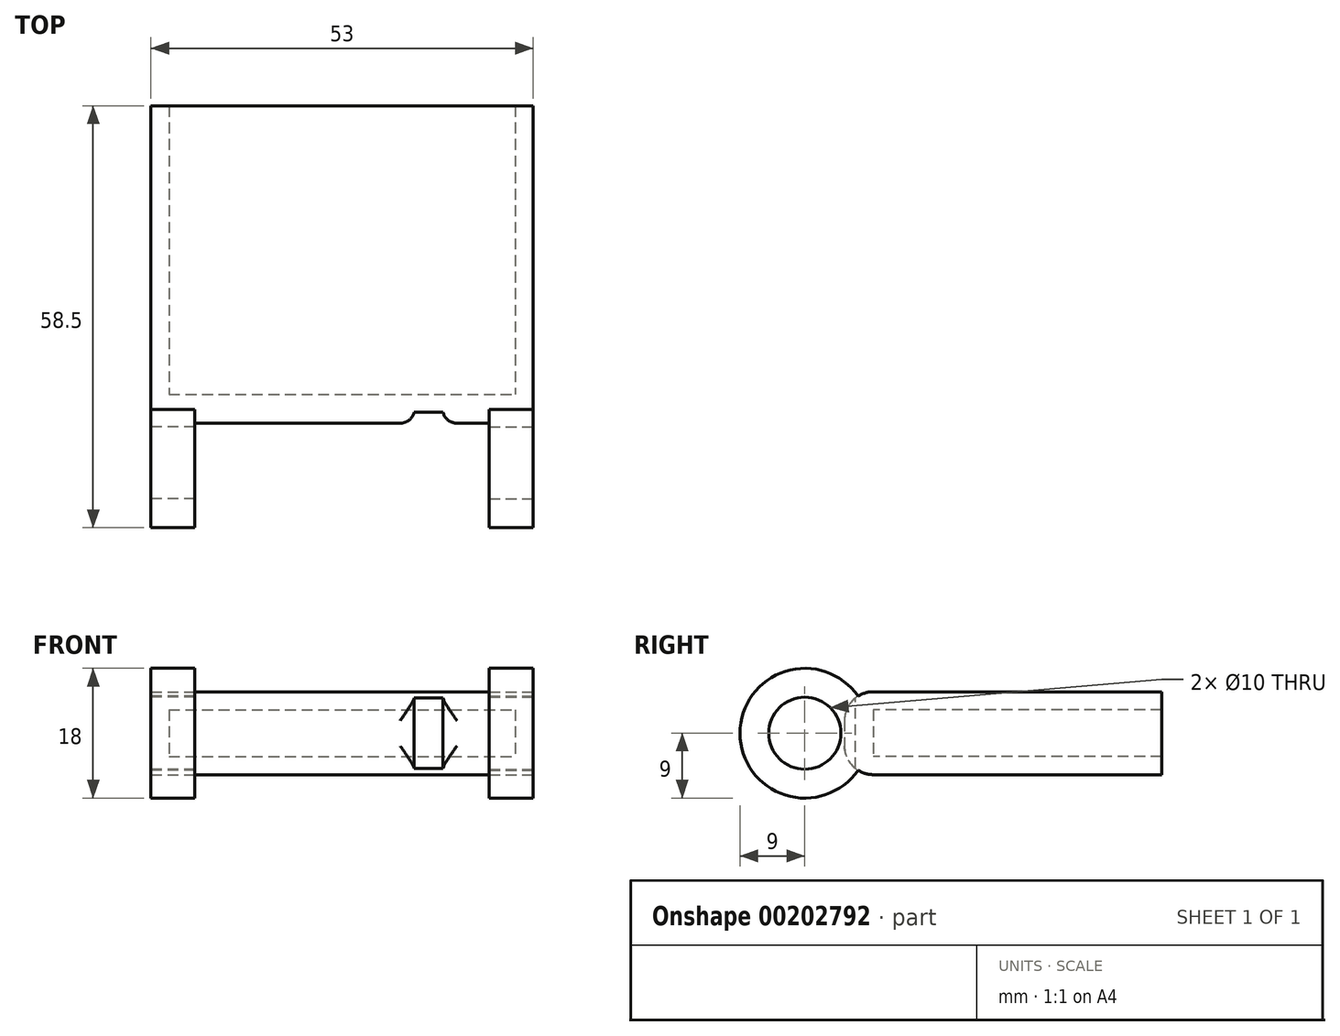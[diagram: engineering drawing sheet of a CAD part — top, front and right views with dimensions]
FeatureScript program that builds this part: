
annotation { "Feature Type Name" : "Feature", "Feature Type Description" : "" }
export const myFeature = defineFeature(function(context is Context, id is Id, definition is map)
    precondition{}
    {
        {
            var Q0;
            Q0=qCreatedBy(makeId("Front.planeOp"),FACE);
            var sketch = newSketch(context, id + "F0", { "sketchPlane" : qUnion([Q0])});
            skLineSegment(sketch, "E0.bottom", {"start": v(-24, 3.25) * mm, "end": v(24, 3.25) * mm});
            skLineSegment(sketch, "E0.top", {"start": v(-24, -3.25) * mm, "end": v(24, -3.25) * mm});
            skLineSegment(sketch, "E0.left", {"start": v(-24, 3.25) * mm, "end": v(-24, -3.25) * mm});
            skLineSegment(sketch, "E0.right", {"start": v(24, 3.25) * mm, "end": v(24, -3.25) * mm});
            skLineSegment(sketch, "E1", {"start": v(0, 3.25) * mm, "end": v(0, -3.25) * mm, "construction": true});
            skLineSegment(sketch, "E2.0", {"start": v(26.5, 5.75) * mm, "end": v(26.5, -5.75) * mm});
            skLineSegment(sketch, "E2.1", {"start": v(-26.5, 5.75) * mm, "end": v(26.5, 5.75) * mm});
            skLineSegment(sketch, "E2.2", {"start": v(-26.5, 5.75) * mm, "end": v(-26.5, -5.75) * mm});
            skLineSegment(sketch, "E2.3", {"start": v(-26.5, -5.75) * mm, "end": v(26.5, -5.75) * mm});
            skSolve(sketch);
        }
        {
            var Q0;
            Q0=makeQuery(id+"F0.imprint","IMPRINT",FACE,{"disambiguationData":[TD([[makeQuery(id+"F0.imprint","IMPRINT",EDGE,{"derivedFrom":sQuery(id+"F0.wireOp",EDGE,"E0.bottom")}),1.0]])]});
            var Q1;
            Q1=makeQuery(id+"F0.imprint","IMPRINT",FACE,{"disambiguationData":[TD([[makeQuery(id+"F0.imprint","IMPRINT",EDGE,{"derivedFrom":sQuery(id+"F0.wireOp",EDGE,"E0.bottom")}),-1.0]])]});
            extrude(context, id + "F1", {"entities" : qUnion([Q0, Q1]), "depth" : 4 * mm});
        }
        {
            var Q0;
            Q0=makeQuery(id+"F0.imprint","IMPRINT",FACE,{"disambiguationData":[TD([[makeQuery(id+"F0.imprint","IMPRINT",EDGE,{"derivedFrom":sQuery(id+"F0.wireOp",EDGE,"E0.bottom")}),1.0]])]});
            extrude(context, id + "F2", {"entities" : qUnion([Q0]), "operationType" : NewBodyOperationType.ADD, "oppositeDirection" : true, "depth" : 40 * mm});
        }
        {
            var Q0;
            {var subQ0=sQuery(id+"F0.wireOp",EDGE,"E2.0");Q0=makeQuery(id+"F2.boolean.opBoolean","MERGE",FACE,{"derivedFrom":[makeQuery(id+"F1.opExtrude","SWEPT_FACE",FACE,{"disambiguationData":[OSD([subQ0])]}),makeQuery(id+"F2.opExtrude","SWEPT_FACE",FACE,{"disambiguationData":[OSD([subQ0])]})]});}
            var sketch = newSketch(context, id + "F3", { "sketchPlane" : qUnion([Q0])});
            skLineSegment(sketch, "E3.bottom", {"start": v(0, 0) * mm, "end": v(-9.5, 0) * mm, "construction": true});
            skLineSegment(sketch, "E3.top", {"start": v(0, -5) * mm, "end": v(-9.5, -5) * mm, "construction": true});
            skLineSegment(sketch, "E3.left", {"start": v(0, 0) * mm, "end": v(0, -5) * mm, "construction": true});
            skLineSegment(sketch, "E3.right", {"start": v(-9.5, 0) * mm, "end": v(-9.5, -5) * mm, "construction": true});
            skCircle(sketch, "E4", {"center": v(-9.5, 0) * mm, "radius": 5 * mm});
            skCircle(sketch, "E5.0", {"center": v(-9.5, 0) * mm, "radius": 9 * mm});
            skSolve(sketch);
        }
        {
            var Q0;
            {var subQ0=sQuery(id+"F0.wireOp",EDGE,"E2.2");Q0=makeQuery(id+"F2.boolean.opBoolean","MERGE",FACE,{"derivedFrom":[makeQuery(id+"F1.opExtrude","SWEPT_FACE",FACE,{"disambiguationData":[OSD([subQ0])]}),makeQuery(id+"F2.opExtrude","SWEPT_FACE",FACE,{"disambiguationData":[OSD([subQ0])]})]});}
            var sketch = newSketch(context, id + "F4", { "sketchPlane" : qUnion([Q0])});
            skCircle(sketch, "E6", {"center": v(9.5, 0) * mm, "radius": 5 * mm});
            skCircle(sketch, "E7", {"center": v(9.5, 0) * mm, "radius": 9 * mm});
            skSolve(sketch);
        }
        {
            var Q0;
            Q0=makeQuery(id+"F4.imprint","IMPRINT",FACE,{"disambiguationData":[TD([[makeQuery(id+"F4.imprint","IMPRINT",EDGE,{"derivedFrom":sQuery(id+"F4.wireOp",EDGE,"E6")}),-1.0]])]});
            extrude(context, id + "F5", {"entities" : qUnion([Q0]), "operationType" : NewBodyOperationType.ADD, "oppositeDirection" : true, "depth" : 6.1 * mm});
        }
        {
            var Q0;
            Q0=makeQuery(id+"F3.imprint","IMPRINT",FACE,{"disambiguationData":[TD([[makeQuery(id+"F3.imprint","IMPRINT",EDGE,{"derivedFrom":sQuery(id+"F3.wireOp",EDGE,"E4")}),-1.0]])]});
            extrude(context, id + "F6", {"entities" : qUnion([Q0]), "operationType" : NewBodyOperationType.ADD, "oppositeDirection" : true, "depth" : 6.1 * mm});
        }
        {
            var Q0;
            Q0=makeQuery(id+"F1.opExtrude","CAP_EDGE",EDGE,{"disambiguationData":[OSD([sQuery(id+"F0.wireOp",EDGE,"E2.1")])],"isStart":false});
            var Q1;
            Q1=makeQuery(id+"F1.opExtrude","CAP_EDGE",EDGE,{"disambiguationData":[OSD([sQuery(id+"F0.wireOp",EDGE,"E2.3")])],"isStart":false});
            fillet(context, id + "F7", {"entities" : qUnion([Q0, Q1]), "radius" : 4 * mm, "tangentPropagation" : true, "allowEdgeOverflow" : false});
        }
        {
            var Q0;
            {var subQ0=sQuery(id+"F0.wireOp",EDGE,"E2.1");Q0=makeQuery(id+"F2.boolean.opBoolean","MERGE",FACE,{"derivedFrom":[makeQuery(id+"F1.opExtrude","SWEPT_FACE",FACE,{"disambiguationData":[OSD([subQ0])]}),makeQuery(id+"F2.opExtrude","SWEPT_FACE",FACE,{"disambiguationData":[OSD([subQ0])]})]});}
            var sketch = newSketch(context, id + "F8", { "sketchPlane" : qUnion([Q0])});
            skLineSegment(sketch, "E8.bottom", {"start": v(0, 0) * mm, "end": v(12, 0) * mm, "construction": true});
            skLineSegment(sketch, "E8.top", {"start": v(0, -2.5) * mm, "end": v(12, -2.5) * mm, "construction": true});
            skLineSegment(sketch, "E8.left", {"start": v(0, 0) * mm, "end": v(0, -2.5) * mm, "construction": true});
            skLineSegment(sketch, "E8.right", {"start": v(12, 0) * mm, "end": v(12, -2.5) * mm, "construction": true});
            skLineSegment(sketch, "E9.bottom", {"start": v(10, -2.5) * mm, "end": v(14, -2.5) * mm});
            skLineSegment(sketch, "E9.top", {"start": v(10, -4.5) * mm, "end": v(14, -4.5) * mm});
            skLineSegment(sketch, "E9.left", {"start": v(10, -2.5) * mm, "end": v(10, -4.5) * mm});
            skLineSegment(sketch, "E9.right", {"start": v(14, -2.5) * mm, "end": v(14, -4.5) * mm});
            skSolve(sketch);
        }
        {
            var Q0;
            Q0=makeQuery(id+"F8.imprint","IMPRINT",FACE,{"disambiguationData":[TD([[makeQuery(id+"F8.imprint","IMPRINT",EDGE,{"derivedFrom":sQuery(id+"F8.wireOp",EDGE,"E9.bottom")}),-1.0]])]});
            extrude(context, id + "F9", {"entities" : qUnion([Q0]), "operationType" : NewBodyOperationType.REMOVE, "oppositeDirection" : true, "depth" : 25 * mm});
        }
        {
            var Q0;
            Q0=makeQuery(id+"F9.boolean.opBoolean","INTERSECT",EDGE,{"derivedFrom":[makeQuery(id+"F1.opExtrude","CAP_FACE",FACE,{"disambiguationData":[OSD([sQuery(id+"F0.wireOp",EDGE,"E2.0"),sQuery(id+"F0.wireOp",EDGE,"E2.1"),sQuery(id+"F0.wireOp",EDGE,"E2.2"),sQuery(id+"F0.wireOp",EDGE,"E2.3")])],"isStart":false}),makeQuery(id+"F9.opExtrude","SWEPT_FACE",FACE,{"disambiguationData":[OSD([sQuery(id+"F8.wireOp",EDGE,"E9.left")])]})]});
            var Q1;
            Q1=makeQuery(id+"F9.boolean.opBoolean","INTERSECT",EDGE,{"derivedFrom":[makeQuery(id+"F1.opExtrude","CAP_FACE",FACE,{"disambiguationData":[OSD([sQuery(id+"F0.wireOp",EDGE,"E2.0"),sQuery(id+"F0.wireOp",EDGE,"E2.1"),sQuery(id+"F0.wireOp",EDGE,"E2.2"),sQuery(id+"F0.wireOp",EDGE,"E2.3")])],"isStart":false}),makeQuery(id+"F9.opExtrude","SWEPT_FACE",FACE,{"disambiguationData":[OSD([sQuery(id+"F8.wireOp",EDGE,"E9.right")])]})]});
            fillet(context, id + "F10", {"entities" : qUnion([Q0, Q1]), "radius" : 2 * mm, "tangentPropagation" : true, "allowEdgeOverflow" : false});
        }
    });
